# Revit family: AFX-Rana-LED_ Flush_Mount-1
name_source: partatom
category: Lighting Fixtures
units: mm (PartAtom-declared; Revit-internal decimal feet)

## family parameters
Cut with Voids When Loaded = No
Host = Face
Light Source = Yes
Part Type = Normal
Room Calculation Point = No
Round Connector Dimension = Use Diameter
Shared = No

## types (1)
- Type Catalog
    Apparent Load = 0 VA
    Assembly Code = D5020200
    Body Finish = AFX - White Steel
    Color Filter = 16777215
    Colour Rendering Index = 90
    Default Elevation = 48"
    Depth = 3"
    Description = Type Catalog
    Diameter = 15 1/2"
    Diffuser Finish = AFX - White Acrylic
    Dimming Lamp Color Temperature Shift = <None>
    Emit Shape Visible in Rendering = No
    Emit from Circle Diameter = 11 1/2"
    Interior Effect Finish = AFX - Gold
    Keynote = 12500
    Manufacturer = AFX Inc
    Model = Type Catalog
    Photometric Web File = RNAF16LAJD1BK_2700K.IES
    Product Documentation Link = Type Catalog
    Revit File Built By = https://servex-us.com
    Sustainability = https://lamprecycle.org
    Tilt Angle = 90.00°
    Type Comments = Rana
    URL = https://www.afxinc.com
    Voltage = 120 V
    Wattage Comments = 15W

## geometry (parser evidence)
native form markers: Sweep x4
no freeform markers — native parametric forms only
